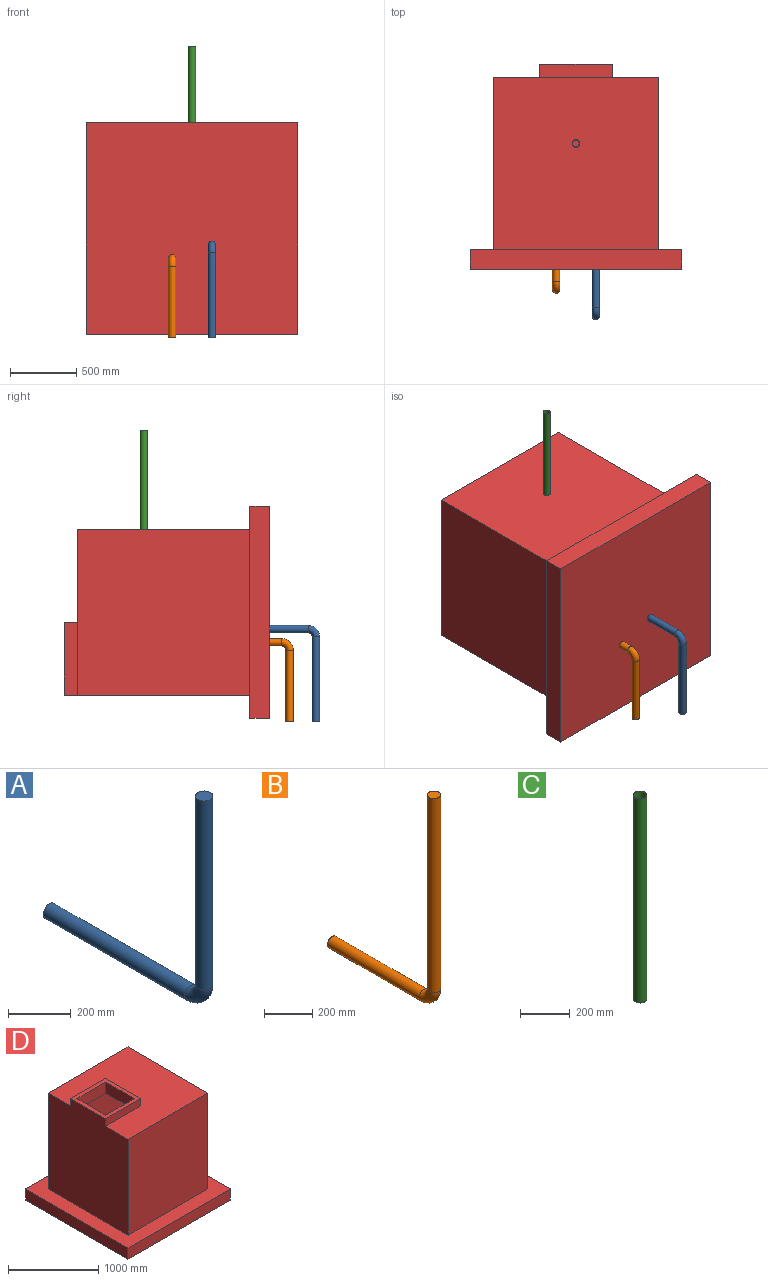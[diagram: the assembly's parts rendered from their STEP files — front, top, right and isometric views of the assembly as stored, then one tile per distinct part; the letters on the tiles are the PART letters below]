
ASSEMBLY  parts=4 mates=3
PART A: 5 faces, bbox 55.7x735.1x835.1 mm
  f0: plane 55.7x55.7mm, normal (0,0,1), area 2436.7mm2, adj f2
  f1: plane 55.7x55.7mm, normal (0,1,0), area 2436.7mm2, adj f4
  f2: cylinder r=27.85mm len=740mm, axis (0,0,-1), area 129490.2mm2, adj f0,f3
  f3: torus R=60mm, axis (1,0,0), area 16492.1mm2, adj f2,f4
  f4: cylinder r=27.85mm len=640mm, axis (0,1,0), area 111991.5mm2, adj f1,f3
PART B: 5 faces, bbox 55.7x635.1x1085.1 mm
  f0: plane 55.7x55.7mm, normal (0,0,1), area 2436.7mm2, adj f2
  f1: plane 55.7x55.7mm, normal (0,1,0), area 2436.7mm2, adj f4
  f2: cylinder r=27.85mm len=990mm, axis (0,0,-1), area 173236.8mm2, adj f0,f3
  f3: torus R=60mm, axis (1,0,0), area 16492.1mm2, adj f2,f4
  f4: cylinder r=27.85mm len=540mm, axis (0,1,0), area 94492.8mm2, adj f1,f3
PART C: 4 faces, bbox 55.7x55.7x1000 mm
  f0: cylinder r=25mm len=1000mm, axis (0,0,-1), area 157079.6mm2, adj f2,f3
  f1: cylinder r=27.85mm len=1000mm, axis (0,0,-1), area 174986.7mm2, adj f2,f3
  f2: plane 55.7x55.7mm, normal (0,0,1), area 473.2mm2, adj f0,f1
  f3: plane 55.7x55.7mm, normal (0,0,-1), area 473.2mm2, adj f0,f1
PART D: 27 faces, bbox 1600x1600x1550 mm
  f0: plane 1250x1250mm, normal (0,0,1), area 1260000mm2, adj f7,f8,f9,f10,f11,f12,f13
  f1: plane 1600x150mm, normal (1,0,0), area 240000mm2, adj f2,f4,f5,f6
  f2: plane 1600x150mm, normal (0,1,0), area 240000mm2, adj f1,f3,f5,f6
  f3: plane 1600x150mm, normal (-1,0,0), area 240000mm2, adj f2,f4,f5,f6
  f4: plane 1600x150mm, normal (0,-1,0), area 240000mm2, adj f1,f3,f5,f6
  f5: plane 1600x1600mm, normal (0,0,-1), area 2555126.6mm2, adj f1,f2,f3,f4,f25,f26
  f6: plane 1600x1600mm, normal (0,0,1), area 997500mm2, adj f1,f2,f3,f4,f7,f8,f9,f10
  f7: plane 1300x1250mm, normal (1,0,0), area 1622563.3mm2, adj f0,f6,f8,f10,f24
  f8: plane 1300x1250mm, normal (0,1,0), area 1625000mm2, adj f0,f6,f7,f9
  f9: plane 1400x1250mm, normal (-1,0,0), area 1680000mm2, adj f0,f6,f8,f10,f11,f13,f14
  f10: plane 1300x1250mm, normal (0,-1,0), area 1625000mm2, adj f0,f6,f7,f9
  f11: plane 550x100mm, normal (0,-1,0), area 55000mm2, adj f0,f9,f12,f14
  f12: plane 550x100mm, normal (1,0,0), area 55000mm2, adj f0,f11,f13,f14
  f13: plane 550x100mm, normal (0,1,0), area 55000mm2, adj f0,f9,f12,f14
  f14: plane 550x550mm, normal (0,0,1), area 100000mm2, adj f9,f11,f12,f13,f20,f21,f22,f23
  f15: plane 1250x1150mm, normal (-1,0,0), area 1435063.3mm2, adj f16,f17,f18,f19,f24
  f16: plane 1250x1150mm, normal (0,1,0), area 1437500mm2, adj f15,f18,f19,f22
  f17: plane 1250x1150mm, normal (0,-1,0), area 1437500mm2, adj f15,f18,f19,f22
  f18: plane 1150x1150mm, normal (0,0,1), area 1317626.6mm2, adj f15,f16,f17,f22,f25,f26
  f19: plane 1150x1150mm, normal (0,0,-1), area 1120000mm2, adj f15,f16,f17,f20,f21,f22,f23
  f20: plane 450x150mm, normal (-1,0,0), area 67500mm2, adj f14,f19,f21,f23
  f21: plane 450x150mm, normal (0,-1,0), area 67500mm2, adj f14,f19,f20,f22
  f22: plane 1400x1150mm, normal (1,0,0), area 1505000mm2, adj f14,f16,f17,f18,f19,f21,f23
  f23: plane 450x150mm, normal (0,1,0), area 67500mm2, adj f14,f19,f20,f22
  f24: cylinder r=27.85mm len=55.7mm, axis (1,0,0), area 8749.3mm2, adj f7,f15
  f25: cylinder r=27.85mm len=150mm, axis (0,0,-1), area 26248mm2, adj f5,f18
  f26: cylinder r=27.85mm len=150mm, axis (0,0,-1), area 26248mm2, adj f5,f18
PLACE A rot(axis=(-1,0,0),90deg) t=(1298.79,-427.3,-435.84)mm
PLACE B rot(axis=(-1,0,0),90deg) t=(998.79,-227.3,-535.84)mm
PLACE C t=(1148.79,872.7,64.16)mm
PLACE D rot(axis=(-0.58,-0.58,-0.58),120deg) t=(1148.79,72.7,-310.84)mm
MATE fastened B.f2 <-> D.f25  axis (0,1,0) through (998.79,822.7,-535.84)mm
MATE fastened A.f2 <-> D.f26  axis (0,1,0) through (1298.79,372.7,-435.84)mm
MATE cylindrical D.f24 <-> C.f0  axis (0,0,1) through (1148.79,872.7,314.16)mm
